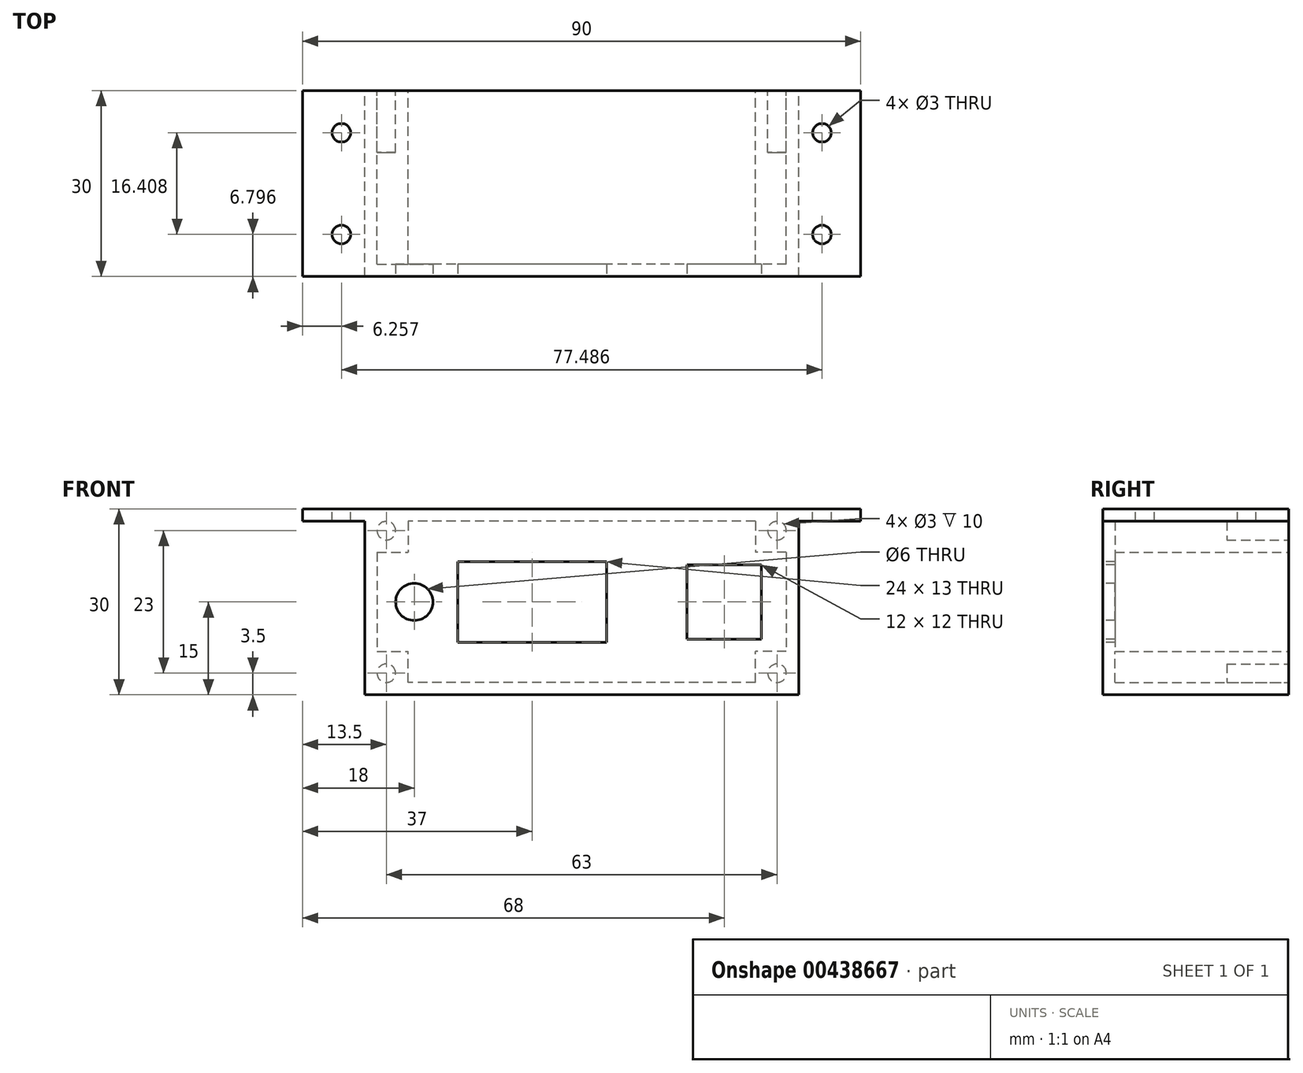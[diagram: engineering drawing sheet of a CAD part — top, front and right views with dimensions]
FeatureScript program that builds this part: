
annotation { "Feature Type Name" : "Feature", "Feature Type Description" : "" }
export const myFeature = defineFeature(function(context is Context, id is Id, definition is map)
    precondition{}
    {
        {
            var Q0;
            Q0=qCreatedBy(makeId("Front.planeOp"),FACE);
            var sketch = newSketch(context, id + "F0", { "sketchPlane" : qUnion([Q0])});
            skLineSegment(sketch, "E0.bottom", {"start": v(35, 15) * mm, "end": v(-35, 15) * mm});
            skLineSegment(sketch, "E0.top", {"start": v(35, -15) * mm, "end": v(-35, -15) * mm});
            skLineSegment(sketch, "E0.left", {"start": v(35, 15) * mm, "end": v(35, -15) * mm});
            skLineSegment(sketch, "E0.right", {"start": v(-35, 15) * mm, "end": v(-35, -15) * mm});
            skPoint(sketch, "E0.middle", {"position": v(0, 0) * mm});
            skSolve(sketch);
        }
        {
            var Q0;
            Q0 = qSketchRegion(id + "F0", true);
            extrude(context, id + "F1", {"entities" : qUnion([Q0]), "depth" : 30 * mm});
        }
        {
            var Q0;
            Q0=makeQuery(id+"F1.opExtrude","CAP_FACE",FACE,{"disambiguationData":[OSD([sQuery(id+"F0.wireOp",EDGE,"E0.bottom"),sQuery(id+"F0.wireOp",EDGE,"E0.top"),sQuery(id+"F0.wireOp",EDGE,"E0.left"),sQuery(id+"F0.wireOp",EDGE,"E0.right")])],"isStart":true});
            shell(context, id + "F2", {"entities" : qUnion([Q0]), "thickness" : 2 * mm});
        }
        {
            var Q0;
            Q0=makeQuery(id+"F1.opExtrude","CAP_FACE",FACE,{"disambiguationData":[OSD([sQuery(id+"F0.wireOp",EDGE,"E0.bottom"),sQuery(id+"F0.wireOp",EDGE,"E0.top"),sQuery(id+"F0.wireOp",EDGE,"E0.left"),sQuery(id+"F0.wireOp",EDGE,"E0.right")])],"isStart":false});
            var sketch = newSketch(context, id + "F3", { "sketchPlane" : qUnion([Q0])});
            skCircle(sketch, "E1", {"center": v(-27, 0) * mm, "radius": 3 * mm});
            skLineSegment(sketch, "E2.bottom", {"start": v(29, 6) * mm, "end": v(17, 6) * mm});
            skLineSegment(sketch, "E2.top", {"start": v(29, -6) * mm, "end": v(17, -6) * mm});
            skLineSegment(sketch, "E2.left", {"start": v(29, 6) * mm, "end": v(29, -6) * mm});
            skLineSegment(sketch, "E2.right", {"start": v(17, 6) * mm, "end": v(17, -6) * mm});
            skPoint(sketch, "E2.middle", {"position": v(23, 0) * mm});
            skLineSegment(sketch, "E3.bottom", {"start": v(4, 6.5) * mm, "end": v(-20, 6.5) * mm});
            skLineSegment(sketch, "E3.top", {"start": v(4, -6.5) * mm, "end": v(-20, -6.5) * mm});
            skLineSegment(sketch, "E3.left", {"start": v(4, 6.5) * mm, "end": v(4, -6.5) * mm});
            skLineSegment(sketch, "E3.right", {"start": v(-20, 6.5) * mm, "end": v(-20, -6.5) * mm});
            skPoint(sketch, "E3.middle", {"position": v(-8, 0) * mm});
            skSolve(sketch);
        }
        {
            var Q0;
            Q0 = qSketchRegion(id + "F3", true);
            extrude(context, id + "F4", {"entities" : qUnion([Q0]), "operationType" : NewBodyOperationType.REMOVE, "endBound" : BoundingType.THROUGH_ALL, "oppositeDirection" : true, "depth" : 25 * mm});
        }
        {
            var Q0;
            Q0=makeQuery(id+"F1.opExtrude","CAP_FACE",FACE,{"disambiguationData":[OSD([sQuery(id+"F0.wireOp",EDGE,"E0.bottom"),sQuery(id+"F0.wireOp",EDGE,"E0.top"),sQuery(id+"F0.wireOp",EDGE,"E0.left"),sQuery(id+"F0.wireOp",EDGE,"E0.right")])],"isStart":true});
            var sketch = newSketch(context, id + "F5", { "sketchPlane" : qUnion([Q0])});
            skLineSegment(sketch, "E4.bottom", {"start": v(-33, 13) * mm, "end": v(-28, 13) * mm});
            skLineSegment(sketch, "E4.top", {"start": v(-33, 8) * mm, "end": v(-28, 8) * mm});
            skLineSegment(sketch, "E4.left", {"start": v(-33, 13) * mm, "end": v(-33, 8) * mm});
            skLineSegment(sketch, "E4.right", {"start": v(-28, 13) * mm, "end": v(-28, 8) * mm});
            skLineSegment(sketch, "E5.MirrorCS", {"start": v(33, 13) * mm, "end": v(28, 13) * mm});
            skLineSegment(sketch, "E6.MirrorCS", {"start": v(33, 13) * mm, "end": v(33, 8) * mm});
            skLineSegment(sketch, "E7.MirrorCS", {"start": v(33, 8) * mm, "end": v(28, 8) * mm});
            skLineSegment(sketch, "E8.MirrorCS", {"start": v(28, 13) * mm, "end": v(28, 8) * mm});
            skLineSegment(sketch, "E9.MirrorCS", {"start": v(33, -13) * mm, "end": v(33, -8) * mm});
            skLineSegment(sketch, "E10.MirrorCS", {"start": v(33, -13) * mm, "end": v(28, -13) * mm});
            skLineSegment(sketch, "E11.MirrorCS", {"start": v(28, -13) * mm, "end": v(28, -8) * mm});
            skLineSegment(sketch, "E12.MirrorCS", {"start": v(33, -8) * mm, "end": v(28, -8) * mm});
            skLineSegment(sketch, "E13.MirrorCS", {"start": v(-28, -13) * mm, "end": v(-28, -8) * mm});
            skLineSegment(sketch, "E14.MirrorCS", {"start": v(-33, -13) * mm, "end": v(-28, -13) * mm});
            skLineSegment(sketch, "E15.MirrorCS", {"start": v(-33, -13) * mm, "end": v(-33, -8) * mm});
            skLineSegment(sketch, "E16.MirrorCS", {"start": v(-33, -8) * mm, "end": v(-28, -8) * mm});
            skSolve(sketch);
        }
        {
            var Q0;
            Q0 = qSketchRegion(id + "F5", true);
            extrude(context, id + "F6", {"entities" : qUnion([Q0]), "operationType" : NewBodyOperationType.ADD, "endBound" : BoundingType.UP_TO_NEXT, "oppositeDirection" : true, "depth" : 25 * mm});
        }
        {
            var Q0;
            Q0=makeQuery(id+"F6.boolean.opBoolean","MERGE",FACE,{"derivedFrom":[makeQuery(id+"F1.opExtrude","CAP_FACE",FACE,{"disambiguationData":[OSD([sQuery(id+"F0.wireOp",EDGE,"E0.bottom"),sQuery(id+"F0.wireOp",EDGE,"E0.top"),sQuery(id+"F0.wireOp",EDGE,"E0.left"),sQuery(id+"F0.wireOp",EDGE,"E0.right")])],"isStart":true}),makeQuery(id+"F6.opExtrude","CAP_FACE",FACE,{"disambiguationData":[OSD([sQuery(id+"F5.wireOp",EDGE,"E4.bottom"),sQuery(id+"F5.wireOp",EDGE,"E4.top"),sQuery(id+"F5.wireOp",EDGE,"E4.left"),sQuery(id+"F5.wireOp",EDGE,"E4.right")])],"isStart":true}),makeQuery(id+"F6.opExtrude","CAP_FACE",FACE,{"disambiguationData":[OSD([sQuery(id+"F5.wireOp",EDGE,"E5.MirrorCS"),sQuery(id+"F5.wireOp",EDGE,"E6.MirrorCS"),sQuery(id+"F5.wireOp",EDGE,"E7.MirrorCS"),sQuery(id+"F5.wireOp",EDGE,"E8.MirrorCS")])],"isStart":true}),makeQuery(id+"F6.opExtrude","CAP_FACE",FACE,{"disambiguationData":[OSD([sQuery(id+"F5.wireOp",EDGE,"E9.MirrorCS"),sQuery(id+"F5.wireOp",EDGE,"E10.MirrorCS"),sQuery(id+"F5.wireOp",EDGE,"E11.MirrorCS"),sQuery(id+"F5.wireOp",EDGE,"E12.MirrorCS")])],"isStart":true}),makeQuery(id+"F6.opExtrude","CAP_FACE",FACE,{"disambiguationData":[OSD([sQuery(id+"F5.wireOp",EDGE,"E13.MirrorCS"),sQuery(id+"F5.wireOp",EDGE,"E14.MirrorCS"),sQuery(id+"F5.wireOp",EDGE,"E15.MirrorCS"),sQuery(id+"F5.wireOp",EDGE,"E16.MirrorCS")])],"isStart":true})]});
            var sketch = newSketch(context, id + "F7", { "sketchPlane" : qUnion([Q0])});
            skLineSegment(sketch, "E17", {"start": v(-28, 8) * mm, "end": v(-35, 15) * mm, "construction": true});
            skCircle(sketch, "E18", {"center": v(-31.5, 11.5) * mm, "radius": 1.5 * mm});
            skCircle(sketch, "E19.MirrorC", {"center": v(31.5, 11.5) * mm, "radius": 1.5 * mm});
            skCircle(sketch, "E20.MirrorC", {"center": v(-31.5, -11.5) * mm, "radius": 1.5 * mm});
            skCircle(sketch, "E21.MirrorC", {"center": v(31.5, -11.5) * mm, "radius": 1.5 * mm});
            skSolve(sketch);
        }
        {
            var Q0;
            Q0 = qSketchRegion(id + "F7", true);
            extrude(context, id + "F8", {"entities" : qUnion([Q0]), "operationType" : NewBodyOperationType.REMOVE, "oppositeDirection" : true, "depth" : 10 * mm});
        }
        {
            var Q0;
            Q0=makeQuery(id+"F1.opExtrude","SWEPT_FACE",FACE,{"disambiguationData":[OSD([sQuery(id+"F0.wireOp",EDGE,"E0.bottom")])]});
            var sketch = newSketch(context, id + "F9", { "sketchPlane" : qUnion([Q0])});
            skLineSegment(sketch, "E22.bottom", {"start": v(-35, 0) * mm, "end": v(-45, 0) * mm});
            skLineSegment(sketch, "E22.top", {"start": v(-35, -30) * mm, "end": v(-45, -30) * mm});
            skLineSegment(sketch, "E22.left", {"start": v(-35, 0) * mm, "end": v(-35, -30) * mm});
            skLineSegment(sketch, "E22.right", {"start": v(-45, 0) * mm, "end": v(-45, -30) * mm});
            skSolve(sketch);
        }
        {
            var Q0;
            Q0 = qSketchRegion(id + "F9", true);
            extrude(context, id + "F10", {"entities" : qUnion([Q0]), "oppositeDirection" : true, "depth" : 2 * mm});
        }
        {
            var Q0;
            Q0=makeQuery(id+"F10.opExtrude","SWEPT_BODY",BODY,{"disambiguationData":[OSD([sQuery(id+"F9.wireOp",EDGE,"E22.bottom"),sQuery(id+"F9.wireOp",EDGE,"E22.top"),sQuery(id+"F9.wireOp",EDGE,"E22.left"),sQuery(id+"F9.wireOp",EDGE,"E22.right")])]});
            var Q1;
            Q1=qCreatedBy(makeId("Right.planeOp"),FACE);
            mirror(context, id + "F11", {"operationType" : NewBodyOperationType.ADD, "entities" : qUnion([Q0]), "mirrorPlane" : qUnion([Q1])});
        }
        {
            var Q0;
            {var subQ0=makeQuery(id+"F10.opExtrude","CAP_FACE",FACE,{"disambiguationData":[OSD([sQuery(id+"F9.wireOp",EDGE,"E22.bottom"),sQuery(id+"F9.wireOp",EDGE,"E22.top"),sQuery(id+"F9.wireOp",EDGE,"E22.left"),sQuery(id+"F9.wireOp",EDGE,"E22.right")])],"isStart":true});Q0=makeQuery(id+"F11.boolean.opBoolean","MERGE",FACE,{"derivedFrom":[makeQuery(id+"F1.opExtrude","SWEPT_FACE",FACE,{"disambiguationData":[OSD([sQuery(id+"F0.wireOp",EDGE,"E0.bottom")])]}),subQ0,makeQuery(id+"F11.opPattern","COPY",FACE,{"derivedFrom":subQ0,"instanceName":"1"})]});}
            var sketch = newSketch(context, id + "F12", { "sketchPlane" : qUnion([Q0])});
            skCircle(sketch, "E23", {"center": v(-38.74, -6.8) * mm, "radius": 1.5 * mm});
            skLineSegment(sketch, "E24", {"start": v(-45, -15) * mm, "end": v(45, -15) * mm, "construction": true});
            skCircle(sketch, "E25.MirrorC", {"center": v(38.74, -6.8) * mm, "radius": 1.5 * mm});
            skCircle(sketch, "E26.MirrorC", {"center": v(-38.74, -23.2) * mm, "radius": 1.5 * mm});
            skCircle(sketch, "E27.MirrorC", {"center": v(38.74, -23.2) * mm, "radius": 1.5 * mm});
            skSolve(sketch);
        }
        {
            var Q0;
            Q0 = qSketchRegion(id + "F12", true);
            extrude(context, id + "F13", {"entities" : qUnion([Q0]), "operationType" : NewBodyOperationType.REMOVE, "endBound" : BoundingType.THROUGH_ALL, "oppositeDirection" : true, "depth" : 25 * mm});
        }
    });
